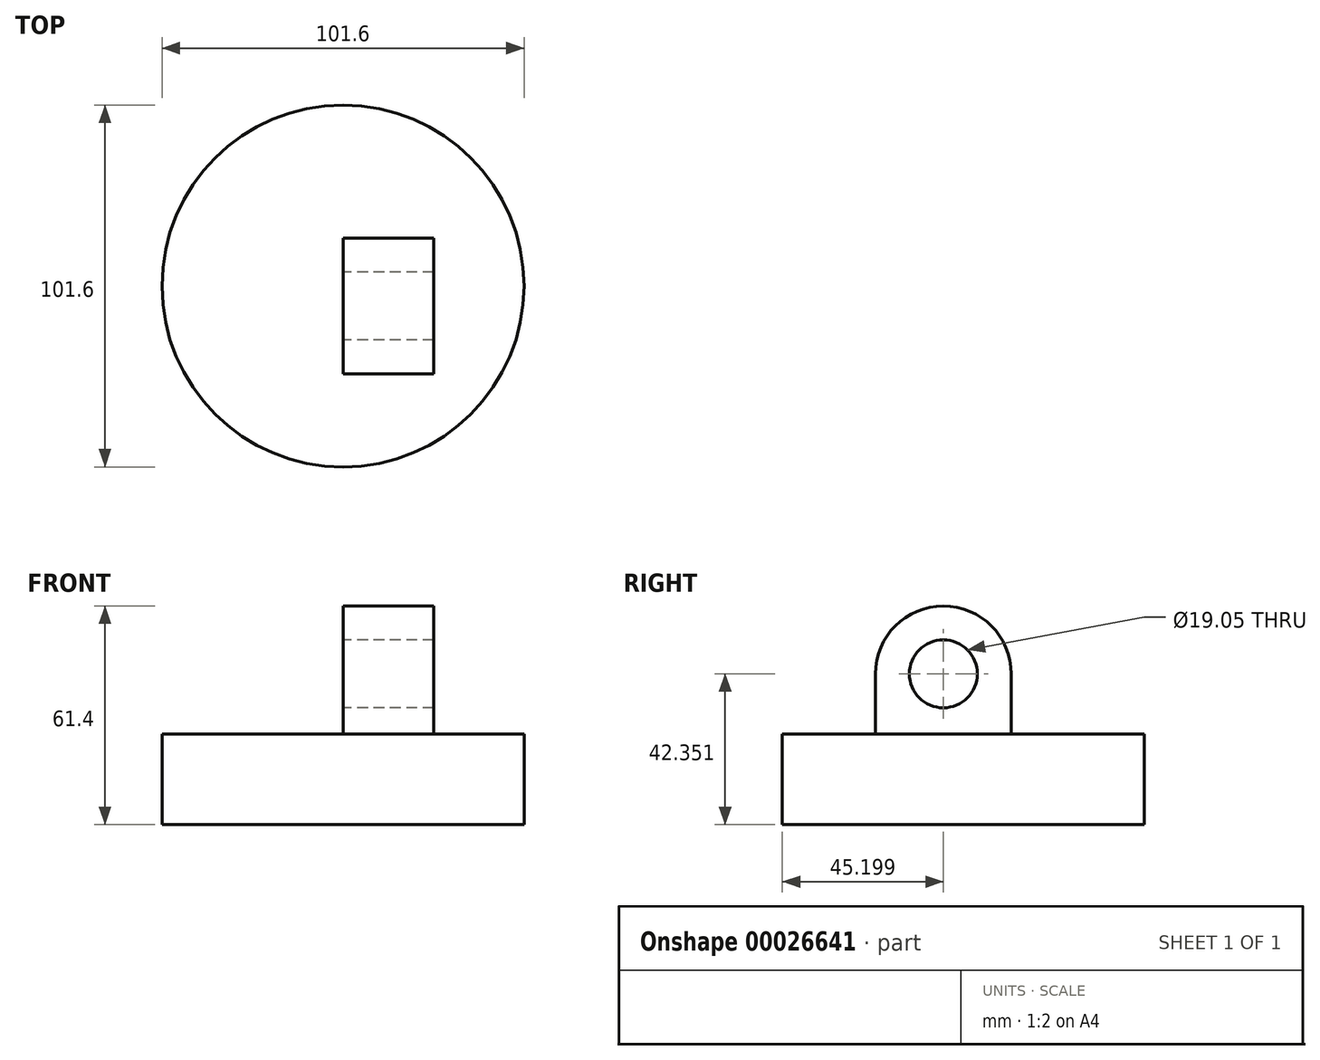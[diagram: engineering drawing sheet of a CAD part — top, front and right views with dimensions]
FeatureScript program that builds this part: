
annotation { "Feature Type Name" : "Feature", "Feature Type Description" : "" }
export const myFeature = defineFeature(function(context is Context, id is Id, definition is map)
    precondition{}
    {
        {
            var Q0;
            Q0=qCreatedBy(makeId("Top.planeOp"),FACE);
            var sketch = newSketch(context, id + "F0", { "sketchPlane" : qUnion([Q0])});
            skCircle(sketch, "E0", {"center": v(0, 0) * mm, "radius": 50.8 * mm});
            skSolve(sketch);
        }
        {
            var Q0;
            Q0=makeQuery(id+"F0.imprint","IMPRINT",FACE,{"disambiguationData":[TD([[makeQuery(id+"F0.imprint","IMPRINT",EDGE,{"derivedFrom":sQuery(id+"F0.wireOp",EDGE,"E0")}),1.0]])]});
            extrude(context, id + "F1", {"entities" : qUnion([Q0]), "depth" : 25.4 * mm});
        }
        {
            var Q0;
            Q0=qCreatedBy(makeId("Right.planeOp"),FACE);
            var sketch = newSketch(context, id + "F2", { "sketchPlane" : qUnion([Q0])});
            skLineSegment(sketch, "E1", {"start": v(-24.65, 4.25) * mm, "end": v(-24.65, 42.35) * mm});
            skLineSegment(sketch, "E2", {"start": v(-24.65, 42.35) * mm, "end": v(13.45, 42.35) * mm});
            skLineSegment(sketch, "E3", {"start": v(13.45, 42.35) * mm, "end": v(13.45, 4.25) * mm});
            skLineSegment(sketch, "E4", {"start": v(13.45, 4.25) * mm, "end": v(-24.65, 4.25) * mm});
            skArc(sketch, "E5", {"start": v(13.45, 42.35) * mm, "mid": v(-5.6, 61.4) * mm, "end": v(-24.65, 42.35) * mm});
            skSolve(sketch);
        }
        {
            var Q0;
            Q0 = qSketchRegion(id + "F2", true);
            extrude(context, id + "F3", {"entities" : qUnion([Q0]), "operationType" : NewBodyOperationType.ADD, "depth" : 25.4 * mm});
        }
        {
            var Q0;
            Q0=makeQuery(id+"F3.opExtrude","CAP_FACE",FACE,{"disambiguationData":[OSD([sQuery(id+"F2.wireOp",EDGE,"E1"),sQuery(id+"F2.wireOp",EDGE,"E3"),sQuery(id+"F2.wireOp",EDGE,"E4"),sQuery(id+"F2.wireOp",EDGE,"E5")])],"isStart":true});
            var sketch = newSketch(context, id + "F4", { "sketchPlane" : qUnion([Q0])});
            skCircle(sketch, "E6", {"center": v(5.6, 42.35) * mm, "radius": 9.53 * mm});
            skPoint(sketch, "E7.orphan", {"position": v(5.6, 61.4) * mm});
            skSolve(sketch);
        }
        {
            var Q0;
            Q0=makeQuery(id+"F4.imprint","IMPRINT",FACE,{"disambiguationData":[TD([[makeQuery(id+"F4.imprint","IMPRINT",EDGE,{"derivedFrom":sQuery(id+"F4.wireOp",EDGE,"E6")}),1.0]])]});
            extrude(context, id + "F5", {"entities" : qUnion([Q0]), "operationType" : NewBodyOperationType.REMOVE, "endBound" : BoundingType.THROUGH_ALL, "oppositeDirection" : true, "depth" : 25.4 * mm});
        }
    });
